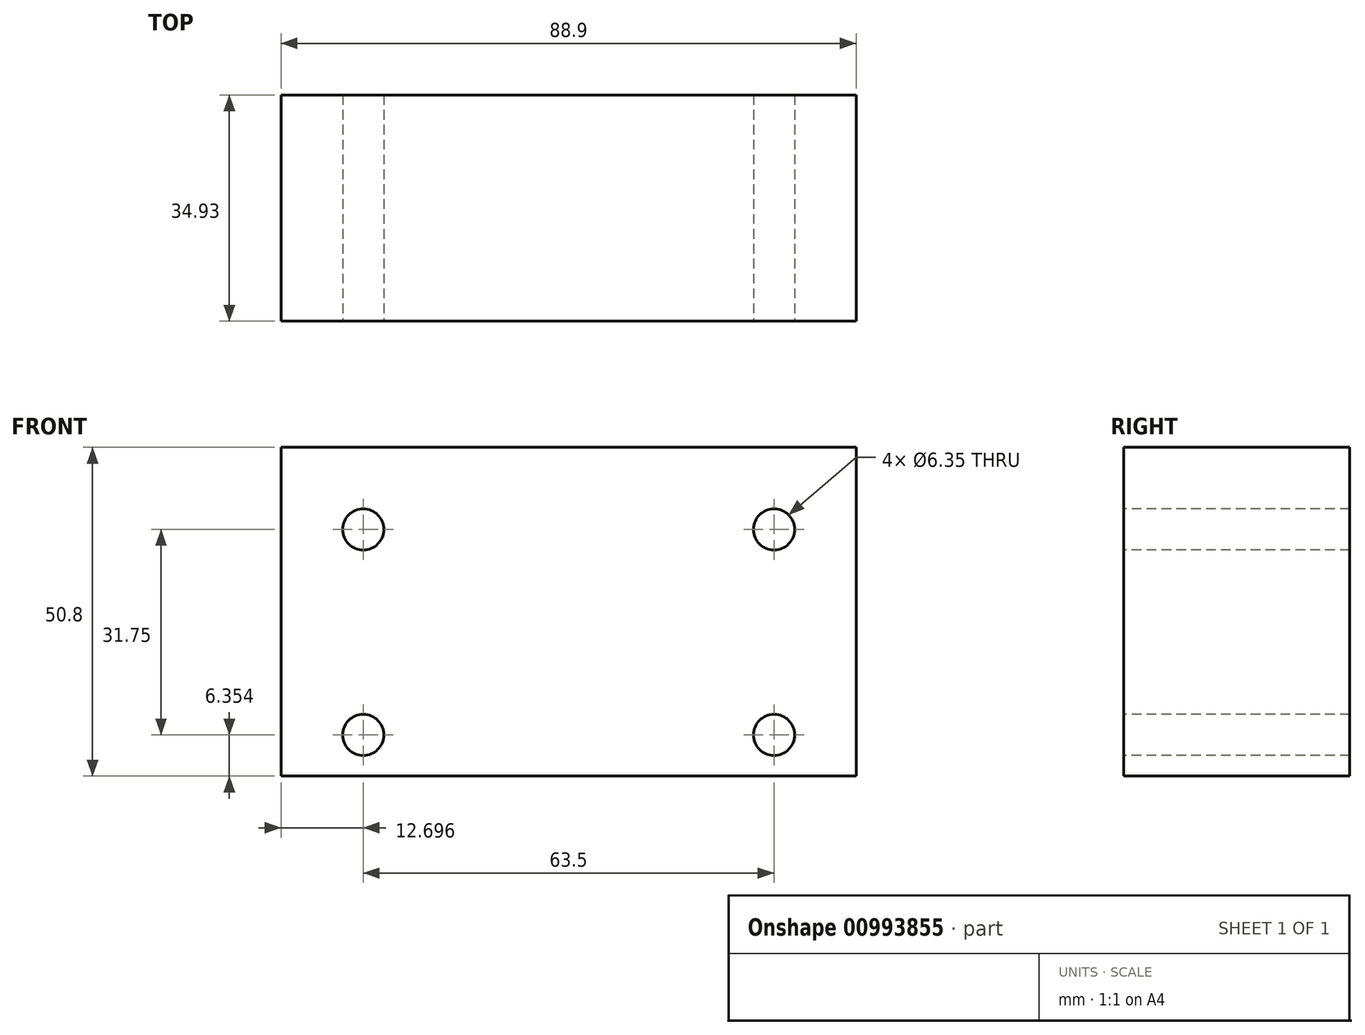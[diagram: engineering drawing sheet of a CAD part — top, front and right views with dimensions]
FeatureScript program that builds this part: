
annotation { "Feature Type Name" : "Feature", "Feature Type Description" : "" }
export const myFeature = defineFeature(function(context is Context, id is Id, definition is map)
    precondition{}
    {
        {
            var Q0;
            Q0=qCreatedBy(makeId("Front.planeOp"),FACE);
            var sketch = newSketch(context, id + "F0", { "sketchPlane" : qUnion([Q0])});
            skLineSegment(sketch, "E0.bottom", {"start": v(-94.55, 80.1) * mm, "end": v(-5.65, 80.1) * mm});
            skLineSegment(sketch, "E0.top", {"start": v(-94.55, 29.3) * mm, "end": v(-5.65, 29.3) * mm});
            skLineSegment(sketch, "E0.left", {"start": v(-94.55, 80.1) * mm, "end": v(-94.55, 29.3) * mm});
            skLineSegment(sketch, "E0.right", {"start": v(-5.65, 80.1) * mm, "end": v(-5.65, 29.3) * mm});
            skSolve(sketch);
        }
        {
            var Q0;
            Q0=qSketchRegion(id+"F0",true);
            var Q1;
            Q1=makeQuery(id+"F0.imprint","IMPRINT",FACE,{"disambiguationData":[TD([[makeQuery(id+"F0.imprint","IMPRINT",EDGE,{"derivedFrom":sQuery(id+"F0.wireOp",EDGE,"E0.bottom")}),-1.0]])]});
            extrude(context, id + "F1", {"entities" : qUnion([Q0, Q1]), "depth" : 34.92 * mm, "offsetDistance" : 25.4 * mm});
        }
        {
            var Q0;
            Q0=makeQuery(id+"F1.opExtrude","CAP_FACE",FACE,{"disambiguationData":[OSD([sQuery(id+"F0.wireOp",EDGE,"E0.bottom"),sQuery(id+"F0.wireOp",EDGE,"E0.top"),sQuery(id+"F0.wireOp",EDGE,"E0.left"),sQuery(id+"F0.wireOp",EDGE,"E0.right")])],"isStart":false});
            var sketch = newSketch(context, id + "F2", { "sketchPlane" : qUnion([Q0])});
            skCircle(sketch, "E1", {"center": v(-81.85, 35.65) * mm, "radius": 3.18 * mm});
            skCircle(sketch, "E2", {"center": v(-81.85, 67.4) * mm, "radius": 3.18 * mm});
            skCircle(sketch, "E3", {"center": v(-18.35, 35.65) * mm, "radius": 3.18 * mm});
            skCircle(sketch, "E4", {"center": v(-18.35, 67.4) * mm, "radius": 3.18 * mm});
            skSolve(sketch);
        }
        {
            var Q0;
            Q0=makeQuery(id+"F2.imprint","IMPRINT",FACE,{"disambiguationData":[TD([[makeQuery(id+"F2.imprint","IMPRINT",EDGE,{"derivedFrom":sQuery(id+"F2.wireOp",EDGE,"E2")}),1.0]])]});
            var Q1;
            Q1=makeQuery(id+"F2.imprint","IMPRINT",FACE,{"disambiguationData":[TD([[makeQuery(id+"F2.imprint","IMPRINT",EDGE,{"derivedFrom":sQuery(id+"F2.wireOp",EDGE,"E1")}),1.0]])]});
            var Q2;
            Q2=makeQuery(id+"F2.imprint","IMPRINT",FACE,{"disambiguationData":[TD([[makeQuery(id+"F2.imprint","IMPRINT",EDGE,{"derivedFrom":sQuery(id+"F2.wireOp",EDGE,"E4")}),1.0]])]});
            var Q3;
            Q3=makeQuery(id+"F2.imprint","IMPRINT",FACE,{"disambiguationData":[TD([[makeQuery(id+"F2.imprint","IMPRINT",EDGE,{"derivedFrom":sQuery(id+"F2.wireOp",EDGE,"E3")}),1.0]])]});
            extrude(context, id + "F3", {"entities" : qUnion([Q0, Q1, Q2, Q3]), "operationType" : NewBodyOperationType.REMOVE, "oppositeDirection" : true, "depth" : 34.92 * mm, "offsetDistance" : 25.4 * mm});
        }
    });
